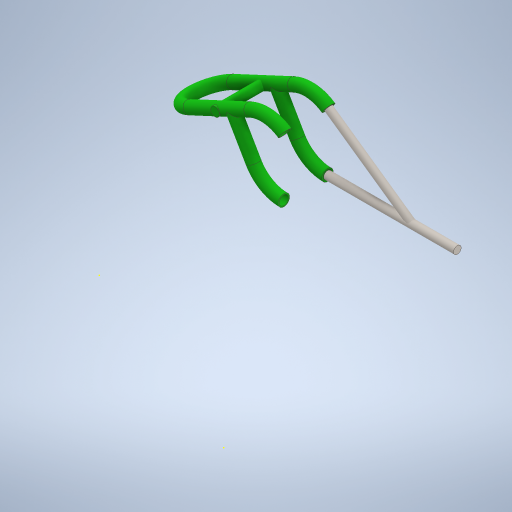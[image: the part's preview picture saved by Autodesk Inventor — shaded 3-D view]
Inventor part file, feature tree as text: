
AUTODESK INVENTOR PART (.ipt)
format: ipt  version: 2024 (Build 280153000, 153)  size: 535,040 bytes
history: native  units: in
note: dims shown in document units (in); Inventor stores cm internally (conversion verified against a paired STEP export)
features: sketch x6, plane x4, extrude x3
ambient origin geometry x8: Origin, YZ Plane, XZ Plane, XY Plane, X Axis, Y Axis, Z Axis, Center Point
bodies: Solid1 (feature_tree), Solid2 (feature_tree), Solid3 (feature_tree), Solid4 (feature_tree), Solid5 (feature_tree), Solid6 (feature_tree), Solid7 (feature_tree), Solid8 (feature_tree), Solid9 (feature_tree), Body1 (feature_tree), Body2 (feature_tree), Body3 (feature_tree), Body4 (feature_tree), Body5 (feature_tree), Body6 (feature_tree), Body7 (feature_tree), Body8 (feature_tree), Body9 (feature_tree)
feature tree (13):
  sketch  "Sketch1"  dims[d0=5.9375in d1=0.0in d2=11.625in d3=0.0in]
  plane  "Work Plane1"
  extrude  "Extrusion1"  Depth=11.625in TaperAngle=0.0deg
  sketch  "Sketch3"  dims[d7=0.1969in d8=0.1969in]
  extrude  "Extrusion2"  Depth=14.875in
  extrude  "Extrusion3"  Depth=0.1969in
  plane  "Work Plane4"
  sketch  "Sketch6"  dims[d11=0.1969in]
  sketch  "Sketch2"  dims[d4=14.875in d5=0.0in d6=1.01in]
  sketch  "Sketch4"  dims[d9=0.1969in]
  sketch  "Sketch5"  dims[d10=0.1969in]
  plane  "Work Plane2"
  plane  "Work Plane3"
